# Revit family: Storage-Teknion-CWRM_Teknion_Reception_Modules-R2016
name_source: partatom
category: Furniture
revit_build: Autodesk Revit 2018 (Build: 20190510_1515(x64)
units: mm (PartAtom-declared; Revit-internal decimal feet)

## family parameters
Always vertical = Yes
Cut with Voids When Loaded = No
OmniClass Number = 23.40.20.00
OmniClass Title = General Furniture and Specialties
Room Calculation Point = No
Shared = Yes
Work Plane-Based = No

## types (5) — shared parameters
Assembly Code = E2020200
Manufacturer = Teknion
Manufacturer Fax = 416.661.4586
Part Number = CWRM
Product Documentation Link = https://assets.teknion.com
Product Line = Teknion Reception
Product Page URL = https://www.teknion.com
Series = Custom Wood
Sustainability Data = https://www.teknion.com
URL = www.teknion.com
Unit Weight URL = http://www.teknion.com
Warranty = http://www.teknion.com

## per-type parameters (varying)
| type | Bottom Drawer Divider Line Hole Depth | Bottom Drawer Height Offset | Box/File | Description | File/File | Horizontal | Horizontal Handles | Model | Not Open | Open | Top Drawer Dividing Line Hole Depth |
| Box/File | 2.593 " | 15.642 " | Yes | Custom Wood Teknion Reception, Storage Modules, 22" Height, Box/File Configuration | No | Yes | Yes | CWRM22B__ | Yes | No | 0.5 " |
| File/File | 2.593 " | 13.902 " | No | Custom Wood Teknion Reception, Storage Modules, 29" Height, File/File Configuration | Yes | Yes | Yes | CWRM29F__ | Yes | No | 0.5 " |
| Pedestal BBF | 2.593 " | 13.902 " | No | Custom Wood Teknion Reception, Storage Modules, 29" Height, Pedestal BBF Configuration | No | Yes | Yes | CWRM29P__ | Yes | No | 2.593 " |
| Closed Cabinet | 0.5 " | 13.902 " | No | Custom Wood Teknion Reception, Storage Modules, Closed Cabinet Configuration | No | No | No | CWRM_C__ | Yes | No | 0.5 " |
| Open | 0.5 " | 13.902 " | No | Custom Wood Teknion Reception, Storage Modules, Open Configuration | No | No | No | CWRM_O__ | No | Yes | 0.5 " |

type visibility flags (boolean, named after types; folded from table):
- Box/File: Yes: (none)
- File/File: Yes: (none)
- Pedestal BBF: Yes: Pedestal BBF
- Closed Cabinet: Yes: Closed Cabinet
- Open: Yes: (none)

## geometry (parser evidence)
native form markers: Sweep x2
no freeform markers — native parametric forms only
